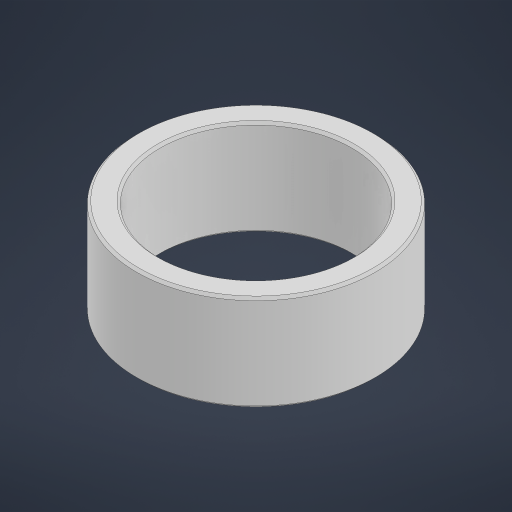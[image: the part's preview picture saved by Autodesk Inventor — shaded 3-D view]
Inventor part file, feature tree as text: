
AUTODESK INVENTOR PART (.ipt)
format: ipt  version: 2023 (Build 270158000, 158)  size: 180,736 bytes
history: native  units: in
note: dims shown in document units (in); Inventor stores cm internally (conversion verified against a paired STEP export)
features: chamfer x1
ambient origin geometry x8: Origin, YZ Plane, XZ Plane, XY Plane, X Axis, Y Axis, Z Axis, Center Point
bodies: Solid1 (feature_tree)
feature tree (1):
  chamfer  "Chamfer1"  [1 undecoded]
note: 1 required parameter value undecoded (feature->parameter linkage not recoverable at this tier; creation-order binding heuristic only, values carry confidence <= 0.55)
